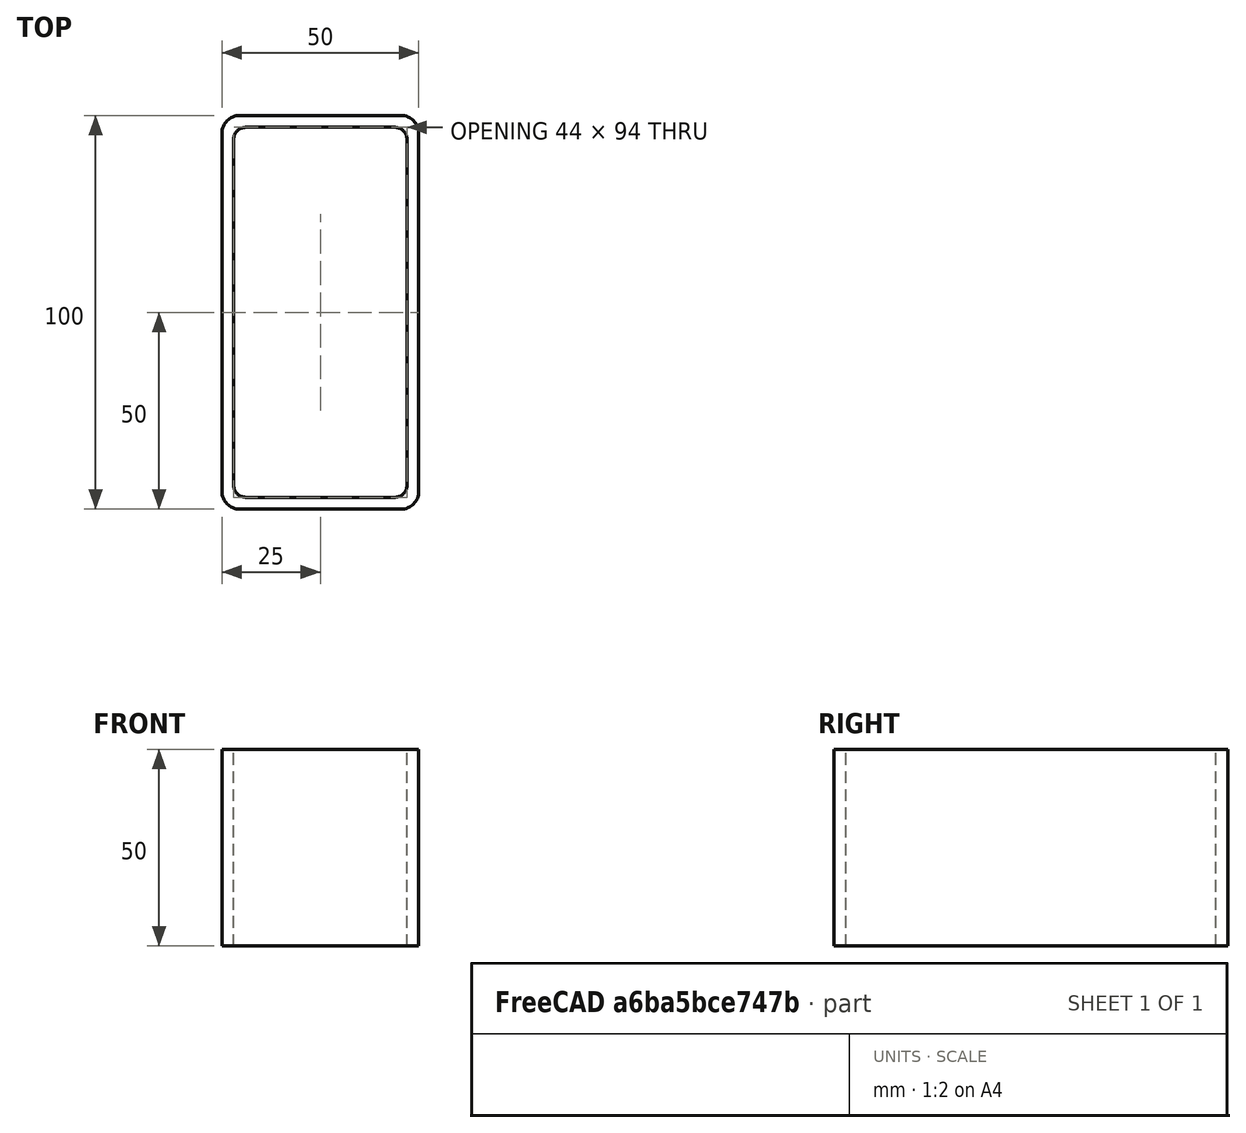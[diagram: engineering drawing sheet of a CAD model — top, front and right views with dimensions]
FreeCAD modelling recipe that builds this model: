
FCSTD DOCUMENT  (FreeCAD 0.15R4671 (Git))
Label: Rectangular hollow section 100x50x3 EN10219 S235JRH
License: All rights reserved
LicenseURL: http://en.wikipedia.org/wiki/All_rights_reserved
objects: Sketcher::SketchObject×1, Part::Extrusion×1
note: 2 computed .brp shape members not serialized (recipe doc carries the construction recipe); baked Part::Feature solids carry a one-line shape summary decoded from their .brp

FEATURE [Sketcher::SketchObject] Sketch
  sketch-geometry (16):
    g0: LineSegment StartX=-19 StartY=47 StartZ=0 EndX=19 EndY=47 EndZ=0
    g1: LineSegment StartX=22 StartY=44 StartZ=0 EndX=22 EndY=-44 EndZ=0
    g2: LineSegment StartX=19 StartY=-47 StartZ=0 EndX=-19 EndY=-47 EndZ=0
    g3: LineSegment StartX=-22 StartY=-44 StartZ=0 EndX=-22 EndY=44 EndZ=0
    g4: LineSegment StartX=-20.5 StartY=50 StartZ=0 EndX=20.5 EndY=50 EndZ=0
    g5: LineSegment StartX=25 StartY=45.5 StartZ=0 EndX=25 EndY=-45.5 EndZ=0
    g6: LineSegment StartX=20.5 StartY=-50 StartZ=0 EndX=-20.5 EndY=-50 EndZ=0
    g7: LineSegment StartX=-25 StartY=-45.5 StartZ=0 EndX=-25 EndY=45.5 EndZ=0
    g8: ArcOfCircle CenterX=-19 CenterY=44 CenterZ=0 NormalX=0 NormalY=0 NormalZ=1 Radius=3 StartAngle=1.5708 EndAngle=3.14159
    g9: ArcOfCircle CenterX=19 CenterY=44 CenterZ=0 NormalX=0 NormalY=0 NormalZ=1 Radius=3 StartAngle=0 EndAngle=1.5708
    g10: ArcOfCircle CenterX=19 CenterY=-44 CenterZ=0 NormalX=0 NormalY=0 NormalZ=1 Radius=3 StartAngle=4.71239 EndAngle=6.28319
    g11: ArcOfCircle CenterX=-19 CenterY=-44 CenterZ=0 NormalX=0 NormalY=0 NormalZ=1 Radius=3 StartAngle=3.14159 EndAngle=4.71239
    g12: ArcOfCircle CenterX=20.5 CenterY=45.5 CenterZ=0 NormalX=0 NormalY=0 NormalZ=1 Radius=4.5 StartAngle=0 EndAngle=1.5708
    g13: ArcOfCircle CenterX=20.5 CenterY=-45.5 CenterZ=0 NormalX=0 NormalY=0 NormalZ=1 Radius=4.5 StartAngle=4.71239 EndAngle=6.28319
    g14: ArcOfCircle CenterX=-20.5 CenterY=-45.5 CenterZ=0 NormalX=0 NormalY=0 NormalZ=1 Radius=4.5 StartAngle=3.14159 EndAngle=4.71239
    g15: ArcOfCircle CenterX=-20.5 CenterY=45.5 CenterZ=0 NormalX=0 NormalY=0 NormalZ=1 Radius=4.5 StartAngle=1.5708 EndAngle=3.14159
  constraints (36):
    c: Horizontal(g2)
    c: Vertical(g3)
    c: Horizontal(g6)
    c: Vertical(g7)
    c: Tangent(g3,g8) = 1.5708
    c: Tangent(g0,g8) = 1.5708
    c: Tangent(g0,g9) = 1.5708
    c: Tangent(g1,g9) = 1.5708
    c: Tangent(g1,g10) = 1.5708
    c: Tangent(g2,g10) = 1.5708
    c: Tangent(g2,g11) = 1.5708
    c: Tangent(g3,g11) = 1.5708
    c: Tangent(g4,g12) = 1.5708
    c: Tangent(g5,g12) = 1.5708
    c: Tangent(g5,g13) = 1.5708
    c: Tangent(g6,g13) = 1.5708
    c: Tangent(g6,g14) = 1.5708
    c: Tangent(g7,g14) = 1.5708
    c: Tangent(g7,g15) = 1.5708
    c: Tangent(g4,g15) = 1.5708
    c: Equal(g9,g8)
    c: Equal(g9,g11)
    c: Equal(g9,g10)
    c: Equal(g12,g15)
    c: Equal(g12,g14)
    c: Equal(g12,g13)
    c: Symmetric(g4,g6,g-1)
    c: Symmetric(g7,g5,g-2)
    c: DistanceY(g4,g6) = -100
    c: DistanceX(g7,g5) = 50
    c: Symmetric(g3,g1,g-2)
    c: Symmetric(g0,g2,g-1)
    c: DistanceY(g0,g4) = 3
    c: DistanceX(g5,g1) = -3
    c: Radius(g9) = 3
    c: Radius(g12) = 4.5
FEATURE [Part::Extrusion] Extrude  label="Rectangular hollow section 100x50x3 EN10219 S235JRH"
  Base = -> Sketch
  Dir = (0,0,50)
  Solid = true
